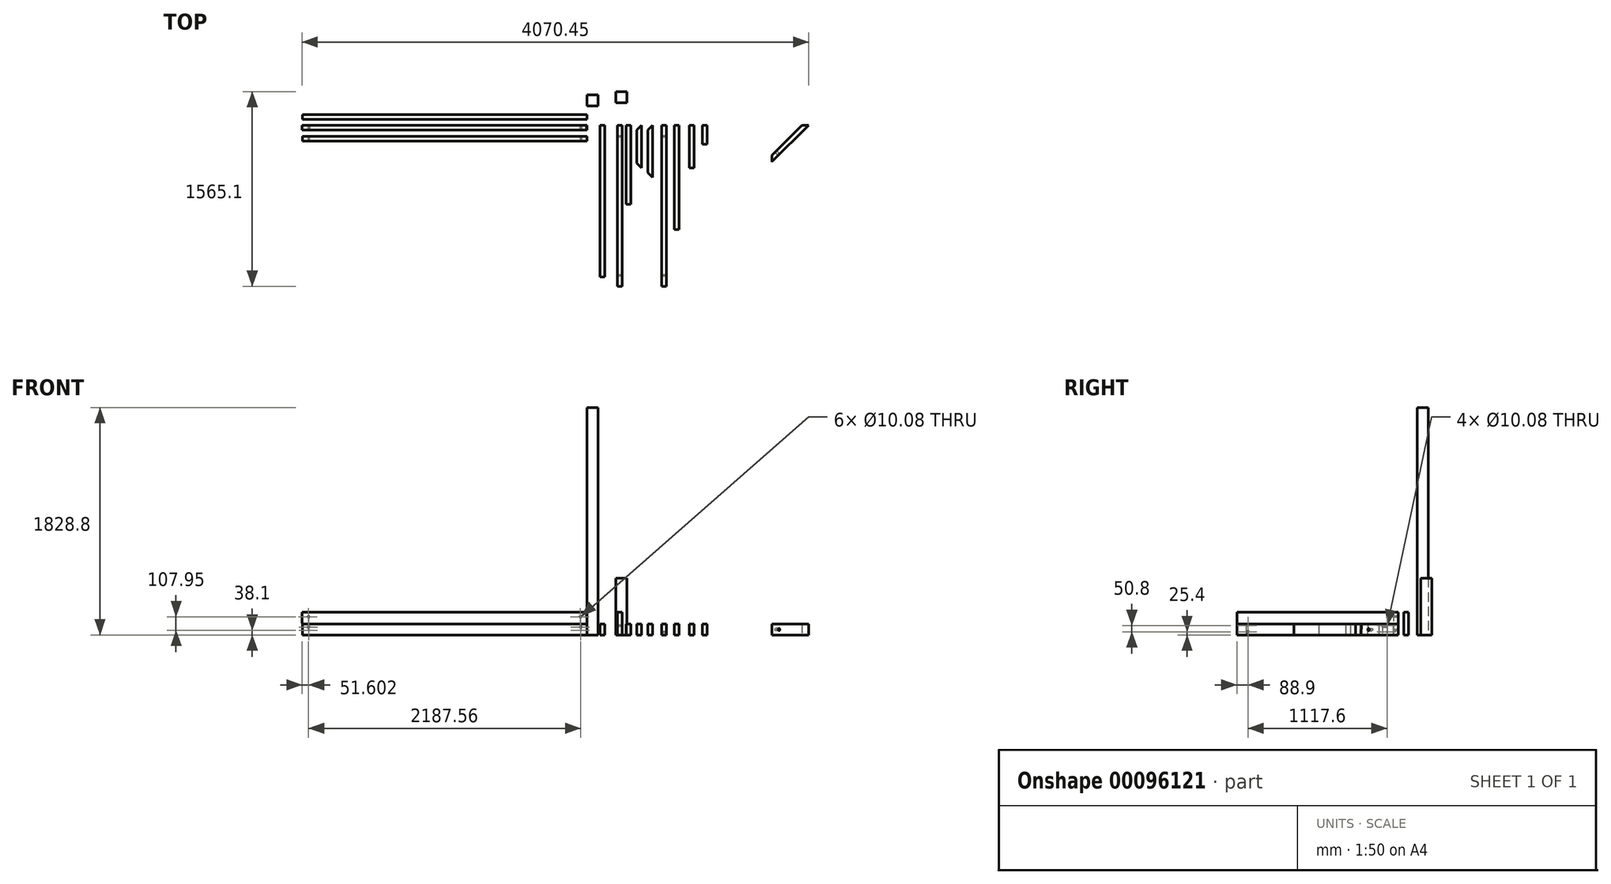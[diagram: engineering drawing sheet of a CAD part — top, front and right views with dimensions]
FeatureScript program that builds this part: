
annotation { "Feature Type Name" : "Feature", "Feature Type Description" : "" }
export const myFeature = defineFeature(function(context is Context, id is Id, definition is map)
    precondition{}
    {
        {
            var Q0;
            Q0=qCreatedBy(makeId("Right.planeOp"),FACE);
            var sketch = newSketch(context, id + "F0", { "sketchPlane" : qUnion([Q0])});
            skLineSegment(sketch, "E0.bottom", {"start": v(0, 0) * mm, "end": v(-38.1, 0) * mm});
            skLineSegment(sketch, "E0.top", {"start": v(0, 184.15) * mm, "end": v(-38.1, 184.15) * mm});
            skLineSegment(sketch, "E0.left", {"start": v(0, 0) * mm, "end": v(0, 184.15) * mm});
            skLineSegment(sketch, "E0.right", {"start": v(-38.1, 0) * mm, "end": v(-38.1, 184.15) * mm});
            skSolve(sketch);
        }
        {
            var Q0;
            Q0=makeQuery(id+"F0.imprint","IMPRINT",FACE,{"disambiguationData":[TD([[makeQuery(id+"F0.imprint","IMPRINT",EDGE,{"derivedFrom":sQuery(id+"F0.wireOp",EDGE,"E0.bottom")}),-1.0]])]});
            extrude(context, id + "F1", {"entities" : qUnion([Q0]), "oppositeDirection" : true, "depth" : 2289.96 * mm});
        }
        {
            var Q0;
            Q0=makeQuery(id+"F1.opExtrude","SWEPT_FACE",FACE,{"disambiguationData":[OSD([sQuery(id+"F0.wireOp",EDGE,"E0.right")])]});
            var sketch = newSketch(context, id + "F2", { "sketchPlane" : qUnion([Q0])});
            skLineSegment(sketch, "E1", {"start": v(0, 0) * mm, "end": v(0, 184.15) * mm});
            skLineSegment(sketch, "E2", {"start": v(0, 184.15) * mm, "end": v(-3.84, 184.15) * mm});
            skLineSegment(sketch, "E3", {"start": v(-3.84, 184.15) * mm, "end": v(0, 0) * mm});
            skLineSegment(sketch, "E4", {"start": v(-2289.96, 184.15) * mm, "end": v(-2286.13, 0) * mm});
            skLineSegment(sketch, "E5", {"start": v(-2286.13, 0) * mm, "end": v(-2289.96, 0) * mm});
            skLineSegment(sketch, "E6", {"start": v(-2289.96, 0) * mm, "end": v(-2289.96, 184.15) * mm});
            skSolve(sketch);
        }
        {
            var Q0;
            Q0=qSketchRegion(id+"F2",true);
            extrude(context, id + "F3", {"entities" : qUnion([Q0]), "operationType" : NewBodyOperationType.REMOVE, "oppositeDirection" : true, "depth" : 38.1 * mm});
        }
        {
            var Q0;
            Q0=qCreatedBy(makeId("Front.planeOp"),FACE);
            var sketch = newSketch(context, id + "F4", { "sketchPlane" : qUnion([Q0])});
            skLineSegment(sketch, "E7.bottom", {"start": v(103.6, 0) * mm, "end": v(141.7, 0) * mm});
            skLineSegment(sketch, "E7.top", {"start": v(103.6, 88.9) * mm, "end": v(141.7, 88.9) * mm});
            skLineSegment(sketch, "E7.left", {"start": v(103.6, 0) * mm, "end": v(103.6, 88.9) * mm});
            skLineSegment(sketch, "E7.right", {"start": v(141.7, 0) * mm, "end": v(141.7, 88.9) * mm});
            skSolve(sketch);
        }
        {
            var Q0;
            Q0=makeQuery(id+"F4.imprint","IMPRINT",FACE,{"disambiguationData":[TD([[makeQuery(id+"F4.imprint","IMPRINT",EDGE,{"derivedFrom":sQuery(id+"F4.wireOp",EDGE,"E7.bottom")}),1.0]])]});
            extrude(context, id + "F5", {"entities" : qUnion([Q0]), "depth" : 1219.2 * mm});
        }
        {
            var Q0;
            Q0=qCreatedBy(makeId("Top.planeOp"),FACE);
            var sketch = newSketch(context, id + "F6", { "sketchPlane" : qUnion([Q0])});
            skLineSegment(sketch, "E8.bottom", {"start": v(0, 155.1) * mm, "end": v(88.9, 155.1) * mm});
            skLineSegment(sketch, "E8.top", {"start": v(0, 244) * mm, "end": v(88.9, 244) * mm});
            skLineSegment(sketch, "E8.left", {"start": v(0, 155.1) * mm, "end": v(0, 244) * mm});
            skLineSegment(sketch, "E8.right", {"start": v(88.9, 155.1) * mm, "end": v(88.9, 244) * mm});
            skSolve(sketch);
        }
        {
            var Q0;
            Q0=qSketchRegion(id+"F6",true);
            extrude(context, id + "F7", {"entities" : qUnion([Q0]), "depth" : 1828.8 * mm});
        }
        {
            var Q0;
            Q0=qCreatedBy(makeId("Front.planeOp"),FACE);
            var sketch = newSketch(context, id + "F8", { "sketchPlane" : qUnion([Q0])});
            skLineSegment(sketch, "E9.bottom", {"start": v(244.55, 0) * mm, "end": v(282.65, 0) * mm});
            skLineSegment(sketch, "E9.top", {"start": v(244.55, 184.15) * mm, "end": v(282.65, 184.15) * mm});
            skLineSegment(sketch, "E9.left", {"start": v(244.55, 0) * mm, "end": v(244.55, 184.15) * mm});
            skLineSegment(sketch, "E9.right", {"start": v(282.65, 0) * mm, "end": v(282.65, 184.15) * mm});
            skSolve(sketch);
        }
        {
            var Q0;
            Q0=makeQuery(id+"F8.imprint","IMPRINT",FACE,{"disambiguationData":[TD([[makeQuery(id+"F8.imprint","IMPRINT",EDGE,{"derivedFrom":sQuery(id+"F8.wireOp",EDGE,"E9.bottom")}),1.0]])]});
            extrude(context, id + "F9", {"entities" : qUnion([Q0]), "depth" : 1295.4 * mm});
        }
        {
            var Q0;
            Q0=qCreatedBy(makeId("Front.planeOp"),FACE);
            var sketch = newSketch(context, id + "F10", { "sketchPlane" : qUnion([Q0])});
            skLineSegment(sketch, "E10.bottom", {"start": v(312.63, 0) * mm, "end": v(350.73, 0) * mm});
            skLineSegment(sketch, "E10.top", {"start": v(312.63, 88.9) * mm, "end": v(350.73, 88.9) * mm});
            skLineSegment(sketch, "E10.left", {"start": v(312.63, 0) * mm, "end": v(312.63, 88.9) * mm});
            skLineSegment(sketch, "E10.right", {"start": v(350.73, 0) * mm, "end": v(350.73, 88.9) * mm});
            skSolve(sketch);
        }
        {
            var Q0;
            Q0=makeQuery(id+"F10.imprint","IMPRINT",FACE,{"disambiguationData":[TD([[makeQuery(id+"F10.imprint","IMPRINT",EDGE,{"derivedFrom":sQuery(id+"F10.wireOp",EDGE,"E10.bottom")}),1.0]])]});
            extrude(context, id + "F11", {"entities" : qUnion([Q0]), "depth" : 635 * mm});
        }
        {
            var Q0;
            Q0=makeQuery(id+"F1.opExtrude","SWEPT_FACE",FACE,{"disambiguationData":[OSD([sQuery(id+"F0.wireOp",EDGE,"E0.right")])]});
            var sketch = newSketch(context, id + "F12", { "sketchPlane" : qUnion([Q0])});
            skPoint(sketch, "E11", {"position": v(-2238.36, 146.05) * mm});
            skPoint(sketch, "E12", {"position": v(-2236.1, 38.1) * mm});
            skPoint(sketch, "E13", {"position": v(-53.85, 146.05) * mm});
            skPoint(sketch, "E14", {"position": v(-51.6, 38.1) * mm});
            skSolve(sketch);
        }
        {
            var Q0;
            Q0=sQuery(id+"F12.wireOp",VERTEX,"E14");
            var Q1;
            Q1=sQuery(id+"F12.wireOp",VERTEX,"E13");
            var Q2;
            Q2=sQuery(id+"F12.wireOp",VERTEX,"E12");
            var Q3;
            Q3=sQuery(id+"F12.wireOp",VERTEX,"E11");
            var Q4;
            Q4=makeQuery(id+"F1.opExtrude","SWEPT_BODY",BODY,{"disambiguationData":[OSD([sQuery(id+"F0.wireOp",EDGE,"E0.bottom"),sQuery(id+"F0.wireOp",EDGE,"E0.top"),sQuery(id+"F0.wireOp",EDGE,"E0.left"),sQuery(id+"F0.wireOp",EDGE,"E0.right")])]});
            hole(context, id + "F13", {"style" : HoleStyle.SIMPLE, "endStyle" : HoleEndStyle.THROUGH, "standardTappedOrClearance" : lookupTablePath({ "standard" : "ANSI", "fit" : "Normal (ASME)", "size" : "3/8", "type" : "Clearance" }), "standardBlindInLast" : lookupTablePath({ "fit" : "Free", "standard" : "ANSI", "size" : "3/8", "type" : "Clearance" }), "holeDiameter" : 10.08 * mm, "locations" : qUnion([Q0, Q1, Q2, Q3]), "scope" : qUnion([Q4]), "isTappedThrough" : true});
        }
        {
            var Q0;
            Q0=makeQuery(id+"F9.opExtrude","SWEPT_FACE",FACE,{"disambiguationData":[OSD([sQuery(id+"F8.wireOp",EDGE,"E9.right")])]});
            var sketch = newSketch(context, id + "F14", { "sketchPlane" : qUnion([Q0])});
            skPoint(sketch, "E15", {"position": v(-1206.5, 76.2) * mm});
            skPoint(sketch, "E16", {"position": v(-88.9, 76.2) * mm});
            skSolve(sketch);
        }
        {
            var Q0;
            Q0=sQuery(id+"F14.wireOp",VERTEX,"4c446d8b-93f8-499f-88b7-25f558c8394a");
            var Q1;
            Q1=sQuery(id+"F14.wireOp",VERTEX,"E15");
            var Q2;
            Q2=sQuery(id+"F14.wireOp",VERTEX,"E16");
            var Q3;
            Q3=sQuery(id+"F14.wireOp",VERTEX,"ef1d34a0-cfd4-4a64-a352-8786edb42035");
            var Q4;
            Q4=makeQuery(id+"F9.opExtrude","SWEPT_BODY",BODY,{"disambiguationData":[OSD([sQuery(id+"F8.wireOp",EDGE,"E9.bottom"),sQuery(id+"F8.wireOp",EDGE,"E9.top"),sQuery(id+"F8.wireOp",EDGE,"E9.left"),sQuery(id+"F8.wireOp",EDGE,"E9.right")])]});
            hole(context, id + "F15", {"style" : HoleStyle.SIMPLE, "endStyle" : HoleEndStyle.THROUGH, "standardTappedOrClearance" : lookupTablePath({ "standard" : "ANSI", "fit" : "Normal (ASME)", "size" : "3/8", "type" : "Clearance" }), "standardBlindInLast" : lookupTablePath({ "fit" : "Free", "standard" : "ANSI", "size" : "3/8", "type" : "Clearance" }), "holeDiameter" : 10.08 * mm, "locations" : qUnion([Q0, Q1, Q2, Q3]), "scope" : qUnion([Q4]), "isTappedThrough" : true});
        }
        {
            var Q0;
            Q0=qCreatedBy(makeId("Front.planeOp"),FACE);
            var sketch = newSketch(context, id + "F16", { "sketchPlane" : qUnion([Q0])});
            skLineSegment(sketch, "E17.bottom", {"start": v(399.52, 0) * mm, "end": v(437.62, 0) * mm});
            skLineSegment(sketch, "E17.top", {"start": v(399.52, 88.9) * mm, "end": v(437.62, 88.9) * mm});
            skLineSegment(sketch, "E17.left", {"start": v(399.52, 0) * mm, "end": v(399.52, 88.9) * mm});
            skLineSegment(sketch, "E17.right", {"start": v(437.62, 0) * mm, "end": v(437.62, 88.9) * mm});
            skSolve(sketch);
        }
        {
            var Q0;
            Q0=makeQuery(id+"F16.imprint","IMPRINT",FACE,{"disambiguationData":[TD([[makeQuery(id+"F16.imprint","IMPRINT",EDGE,{"derivedFrom":sQuery(id+"F16.wireOp",EDGE,"E17.bottom")}),1.0]])]});
            extrude(context, id + "F17", {"entities" : qUnion([Q0]), "depth" : 342.9 * mm});
        }
        {
            var Q0;
            Q0=makeQuery(id+"F17.opExtrude","SWEPT_FACE",FACE,{"disambiguationData":[OSD([sQuery(id+"F16.wireOp",EDGE,"E17.top")])]});
            var sketch = newSketch(context, id + "F18", { "sketchPlane" : qUnion([Q0])});
            skLineSegment(sketch, "E18", {"start": v(437.62, 0) * mm, "end": v(399.52, -38.1) * mm});
            skLineSegment(sketch, "E19", {"start": v(399.52, -38.1) * mm, "end": v(399.52, 0) * mm});
            skLineSegment(sketch, "E20", {"start": v(399.52, 0) * mm, "end": v(437.62, 0) * mm});
            skLineSegment(sketch, "E21", {"start": v(437.62, -342.9) * mm, "end": v(399.52, -304.8) * mm});
            skLineSegment(sketch, "E22", {"start": v(399.52, -304.8) * mm, "end": v(399.52, -342.9) * mm});
            skLineSegment(sketch, "E23", {"start": v(399.52, -342.9) * mm, "end": v(437.62, -342.9) * mm});
            skSolve(sketch);
        }
        {
            var Q0;
            Q0=makeQuery(id+"F18.imprint","IMPRINT",FACE,{"disambiguationData":[TD([[makeQuery(id+"F18.imprint","IMPRINT",EDGE,{"derivedFrom":sQuery(id+"F18.wireOp",EDGE,"E18")}),-1.0]])]});
            var Q1;
            Q1=makeQuery(id+"F18.imprint","IMPRINT",FACE,{"disambiguationData":[TD([[makeQuery(id+"F18.imprint","IMPRINT",EDGE,{"derivedFrom":sQuery(id+"F18.wireOp",EDGE,"E21")}),1.0]])]});
            extrude(context, id + "F19", {"entities" : qUnion([Q0, Q1]), "operationType" : NewBodyOperationType.REMOVE, "oppositeDirection" : true, "depth" : 88.9 * mm});
        }
        {
            var Q0;
            Q0=qCreatedBy(makeId("Top.planeOp"),FACE);
            var sketch = newSketch(context, id + "F20", { "sketchPlane" : qUnion([Q0])});
            skLineSegment(sketch, "E24.bottom", {"start": v(230.08, 180.8) * mm, "end": v(318.98, 180.8) * mm});
            skLineSegment(sketch, "E24.top", {"start": v(230.08, 269.7) * mm, "end": v(318.98, 269.7) * mm});
            skLineSegment(sketch, "E24.left", {"start": v(230.08, 180.8) * mm, "end": v(230.08, 269.7) * mm});
            skLineSegment(sketch, "E24.right", {"start": v(318.98, 180.8) * mm, "end": v(318.98, 269.7) * mm});
            skSolve(sketch);
        }
        {
            var Q0;
            Q0=makeQuery(id+"F20.imprint","IMPRINT",FACE,{"disambiguationData":[TD([[makeQuery(id+"F20.imprint","IMPRINT",EDGE,{"derivedFrom":sQuery(id+"F20.wireOp",EDGE,"E24.bottom")}),1.0]])]});
            extrude(context, id + "F21", {"entities" : qUnion([Q0]), "depth" : 457.2 * mm});
        }
        {
            var Q0;
            Q0=qCreatedBy(makeId("Front.planeOp"),FACE);
            var sketch = newSketch(context, id + "F22", { "sketchPlane" : qUnion([Q0])});
            skLineSegment(sketch, "E25.bottom", {"start": v(487.43, 0) * mm, "end": v(525.53, 0) * mm});
            skLineSegment(sketch, "E25.top", {"start": v(487.43, 88.9) * mm, "end": v(525.53, 88.9) * mm});
            skLineSegment(sketch, "E25.left", {"start": v(487.43, 0) * mm, "end": v(487.43, 88.9) * mm});
            skLineSegment(sketch, "E25.right", {"start": v(525.53, 0) * mm, "end": v(525.53, 88.9) * mm});
            skSolve(sketch);
        }
        {
            var Q0;
            Q0=makeQuery(id+"F22.imprint","IMPRINT",FACE,{"disambiguationData":[TD([[makeQuery(id+"F22.imprint","IMPRINT",EDGE,{"derivedFrom":sQuery(id+"F22.wireOp",EDGE,"E25.bottom")}),1.0]])]});
            extrude(context, id + "F23", {"entities" : qUnion([Q0]), "depth" : 419.1 * mm});
        }
        {
            var Q0;
            Q0=makeQuery(id+"F23.opExtrude","SWEPT_FACE",FACE,{"disambiguationData":[OSD([sQuery(id+"F22.wireOp",EDGE,"E25.top")])]});
            var sketch = newSketch(context, id + "F24", { "sketchPlane" : qUnion([Q0])});
            skLineSegment(sketch, "E26", {"start": v(525.53, 0) * mm, "end": v(525.53, 38.1) * mm});
            skLineSegment(sketch, "E27", {"start": v(525.53, 38.1) * mm, "end": v(487.43, 0) * mm});
            skLineSegment(sketch, "E28", {"start": v(487.43, 0) * mm, "end": v(525.53, 0) * mm});
            skLineSegment(sketch, "E29", {"start": v(525.53, -419.1) * mm, "end": v(525.53, -457.2) * mm});
            skLineSegment(sketch, "E30", {"start": v(525.53, -457.2) * mm, "end": v(487.43, -419.1) * mm});
            skLineSegment(sketch, "E31", {"start": v(487.43, -419.1) * mm, "end": v(525.53, -419.1) * mm});
            skSolve(sketch);
        }
        {
            var Q0;
            Q0=makeQuery(id+"F24.imprint","IMPRINT",FACE,{"disambiguationData":[TD([[makeQuery(id+"F24.imprint","IMPRINT",EDGE,{"derivedFrom":sQuery(id+"F24.wireOp",EDGE,"E26")}),1.0]])]});
            var Q1;
            Q1=makeQuery(id+"F24.imprint","IMPRINT",FACE,{"disambiguationData":[TD([[makeQuery(id+"F24.imprint","IMPRINT",EDGE,{"derivedFrom":sQuery(id+"F24.wireOp",EDGE,"E29")}),-1.0]])]});
            extrude(context, id + "F25", {"entities" : qUnion([Q0, Q1]), "oppositeDirection" : true, "depth" : 88.9 * mm});
        }
        {
            var Q0;
            Q0=makeQuery(id+"F25.opExtrude","SWEPT_BODY",BODY,{"disambiguationData":[OSD([sQuery(id+"F24.wireOp",EDGE,"E29"),sQuery(id+"F24.wireOp",EDGE,"E30"),sQuery(id+"F24.wireOp",EDGE,"E31")])]});
            deleteBodies(context, id + "F26", {"entities" : qUnion([Q0])});
        }
        {
            var Q0;
            Q0=makeQuery(id+"F25.opExtrude","SWEPT_BODY",BODY,{"disambiguationData":[OSD([sQuery(id+"F24.wireOp",EDGE,"E26"),sQuery(id+"F24.wireOp",EDGE,"E27"),sQuery(id+"F24.wireOp",EDGE,"E28")])]});
            deleteBodies(context, id + "F27", {"entities" : qUnion([Q0])});
        }
        {
            var Q0;
            Q0=makeQuery(id+"F23.opExtrude","SWEPT_FACE",FACE,{"disambiguationData":[OSD([sQuery(id+"F22.wireOp",EDGE,"E25.top")])]});
            var sketch = newSketch(context, id + "F28", { "sketchPlane" : qUnion([Q0])});
            skLineSegment(sketch, "E32", {"start": v(525.53, 0) * mm, "end": v(487.43, -38.1) * mm});
            skLineSegment(sketch, "E33", {"start": v(487.43, -38.1) * mm, "end": v(487.43, 0) * mm});
            skLineSegment(sketch, "E34", {"start": v(487.43, 0) * mm, "end": v(525.53, 0) * mm});
            skLineSegment(sketch, "E35", {"start": v(525.53, -419.1) * mm, "end": v(487.43, -381) * mm});
            skLineSegment(sketch, "E36", {"start": v(487.43, -381) * mm, "end": v(487.43, -419.1) * mm});
            skLineSegment(sketch, "E37", {"start": v(487.43, -419.1) * mm, "end": v(525.53, -419.1) * mm});
            skSolve(sketch);
        }
        {
            var Q0;
            Q0=makeQuery(id+"F28.imprint","IMPRINT",FACE,{"disambiguationData":[TD([[makeQuery(id+"F28.imprint","IMPRINT",EDGE,{"derivedFrom":sQuery(id+"F28.wireOp",EDGE,"E32")}),-1.0]])]});
            var Q1;
            Q1=makeQuery(id+"F28.imprint","IMPRINT",FACE,{"disambiguationData":[TD([[makeQuery(id+"F28.imprint","IMPRINT",EDGE,{"derivedFrom":sQuery(id+"F28.wireOp",EDGE,"E35")}),1.0]])]});
            extrude(context, id + "F29", {"entities" : qUnion([Q0, Q1]), "operationType" : NewBodyOperationType.REMOVE, "oppositeDirection" : true, "depth" : 88.9 * mm});
        }
        {
            var Q0;
            Q0=qCreatedBy(makeId("Right.planeOp"),FACE);
            var sketch = newSketch(context, id + "F30", { "sketchPlane" : qUnion([Q0])});
            skLineSegment(sketch, "E38.bottom", {"start": v(-88.17, 0) * mm, "end": v(-126.27, 0) * mm});
            skLineSegment(sketch, "E38.top", {"start": v(-88.17, 88.9) * mm, "end": v(-126.27, 88.9) * mm});
            skLineSegment(sketch, "E38.left", {"start": v(-88.17, 0) * mm, "end": v(-88.17, 88.9) * mm});
            skLineSegment(sketch, "E38.right", {"start": v(-126.27, 0) * mm, "end": v(-126.27, 88.9) * mm});
            skSolve(sketch);
        }
        {
            var Q0;
            Q0=makeQuery(id+"F30.imprint","IMPRINT",FACE,{"disambiguationData":[TD([[makeQuery(id+"F30.imprint","IMPRINT",EDGE,{"derivedFrom":sQuery(id+"F30.wireOp",EDGE,"E38.bottom")}),-1.0]])]});
            extrude(context, id + "F31", {"entities" : qUnion([Q0]), "oppositeDirection" : true, "depth" : 2287.9 * mm});
        }
        {
            var Q0;
            Q0=makeQuery(id+"F31.opExtrude","SWEPT_FACE",FACE,{"disambiguationData":[OSD([sQuery(id+"F30.wireOp",EDGE,"E38.right")])]});
            var sketch = newSketch(context, id + "F32", { "sketchPlane" : qUnion([Q0])});
            skLineSegment(sketch, "E39", {"start": v(0, 0) * mm, "end": v(-1.85, 88.9) * mm});
            skLineSegment(sketch, "E40", {"start": v(-1.85, 88.9) * mm, "end": v(0, 88.9) * mm});
            skLineSegment(sketch, "E41", {"start": v(0, 88.9) * mm, "end": v(0, 0) * mm});
            skLineSegment(sketch, "E42", {"start": v(-2287.91, 88.9) * mm, "end": v(-2286.06, 0) * mm});
            skLineSegment(sketch, "E43", {"start": v(-2286.06, 0) * mm, "end": v(-2287.91, 0) * mm});
            skLineSegment(sketch, "E44", {"start": v(-2287.91, 0) * mm, "end": v(-2287.91, 88.9) * mm});
            skSolve(sketch);
        }
        {
            var Q0;
            Q0=makeQuery(id+"F32.imprint","IMPRINT",FACE,{"disambiguationData":[TD([[makeQuery(id+"F32.imprint","IMPRINT",EDGE,{"derivedFrom":sQuery(id+"F32.wireOp",EDGE,"E42")}),-1.0]])]});
            var Q1;
            Q1=makeQuery(id+"F32.imprint","IMPRINT",FACE,{"disambiguationData":[TD([[makeQuery(id+"F32.imprint","IMPRINT",EDGE,{"derivedFrom":sQuery(id+"F32.wireOp",EDGE,"E39")}),-1.0]])]});
            extrude(context, id + "F33", {"entities" : qUnion([Q0, Q1]), "operationType" : NewBodyOperationType.REMOVE, "oppositeDirection" : true, "depth" : 38.1 * mm});
        }
        {
            var Q0;
            Q0=qCreatedBy(makeId("Front.planeOp"),FACE);
            var sketch = newSketch(context, id + "F34", { "sketchPlane" : qUnion([Q0])});
            skLineSegment(sketch, "E45.bottom", {"start": v(600.5, 0) * mm, "end": v(638.6, 0) * mm});
            skLineSegment(sketch, "E45.top", {"start": v(600.5, 88.9) * mm, "end": v(638.6, 88.9) * mm});
            skLineSegment(sketch, "E45.left", {"start": v(600.5, 0) * mm, "end": v(600.5, 88.9) * mm});
            skLineSegment(sketch, "E45.right", {"start": v(638.6, 0) * mm, "end": v(638.6, 88.9) * mm});
            skSolve(sketch);
        }
        {
            var Q0;
            Q0=makeQuery(id+"F34.imprint","IMPRINT",FACE,{"disambiguationData":[TD([[makeQuery(id+"F34.imprint","IMPRINT",EDGE,{"derivedFrom":sQuery(id+"F34.wireOp",EDGE,"E45.bottom")}),1.0]])]});
            extrude(context, id + "F35", {"entities" : qUnion([Q0]), "depth" : 1295.4 * mm});
        }
        {
            var Q0;
            Q0=makeQuery(id+"F31.opExtrude","SWEPT_FACE",FACE,{"disambiguationData":[OSD([sQuery(id+"F30.wireOp",EDGE,"E38.right")])]});
            var sketch = newSketch(context, id + "F36", { "sketchPlane" : qUnion([Q0])});
            skPoint(sketch, "E46", {"position": v(-2237.11, 63.5) * mm});
            skPoint(sketch, "E47", {"position": v(-50.8, 63.5) * mm});
            skSolve(sketch);
        }
        {
            var Q0;
            Q0=sQuery(id+"F36.wireOp",VERTEX,"E46");
            var Q1;
            Q1=sQuery(id+"F36.wireOp",VERTEX,"E47");
            var Q2;
            Q2=makeQuery(id+"F31.opExtrude","SWEPT_BODY",BODY,{"disambiguationData":[OSD([sQuery(id+"F30.wireOp",EDGE,"E38.bottom"),sQuery(id+"F30.wireOp",EDGE,"E38.top"),sQuery(id+"F30.wireOp",EDGE,"E38.left"),sQuery(id+"F30.wireOp",EDGE,"E38.right")])]});
            hole(context, id + "F37", {"style" : HoleStyle.SIMPLE, "endStyle" : HoleEndStyle.THROUGH, "standardTappedOrClearance" : lookupTablePath({ "standard" : "ANSI", "fit" : "Normal (ASME)", "size" : "3/8", "type" : "Clearance" }), "standardBlindInLast" : lookupTablePath({ "fit" : "Free", "standard" : "ANSI", "size" : "3/8", "type" : "Clearance" }), "holeDiameter" : 10.08 * mm, "locations" : qUnion([Q0, Q1]), "scope" : qUnion([Q2]), "isTappedThrough" : true});
        }
        {
            var Q0;
            Q0=makeQuery(id+"F35.opExtrude","SWEPT_FACE",FACE,{"disambiguationData":[OSD([sQuery(id+"F34.wireOp",EDGE,"E45.right")])]});
            var sketch = newSketch(context, id + "F38", { "sketchPlane" : qUnion([Q0])});
            skPoint(sketch, "E48", {"position": v(-1206.5, 25.4) * mm});
            skPoint(sketch, "E49", {"position": v(-88.9, 25.4) * mm});
            skSolve(sketch);
        }
        {
            var Q0;
            Q0=sQuery(id+"F38.wireOp",VERTEX,"E49");
            var Q1;
            Q1=sQuery(id+"F38.wireOp",VERTEX,"E48");
            var Q2;
            Q2=makeQuery(id+"F35.opExtrude","SWEPT_BODY",BODY,{"disambiguationData":[OSD([sQuery(id+"F34.wireOp",EDGE,"E45.bottom"),sQuery(id+"F34.wireOp",EDGE,"E45.top"),sQuery(id+"F34.wireOp",EDGE,"E45.left"),sQuery(id+"F34.wireOp",EDGE,"E45.right")])]});
            hole(context, id + "F39", {"style" : HoleStyle.SIMPLE, "endStyle" : HoleEndStyle.THROUGH, "standardTappedOrClearance" : lookupTablePath({ "standard" : "ANSI", "fit" : "Normal (ASME)", "size" : "3/8", "type" : "Clearance" }), "standardBlindInLast" : lookupTablePath({ "fit" : "Free", "standard" : "ANSI", "size" : "3/8", "type" : "Clearance" }), "holeDiameter" : 10.08 * mm, "locations" : qUnion([Q0, Q1]), "scope" : qUnion([Q2]), "isTappedThrough" : true});
        }
        {
            var Q0;
            Q0=qCreatedBy(makeId("Front.planeOp"),FACE);
            var sketch = newSketch(context, id + "F40", { "sketchPlane" : qUnion([Q0])});
            skLineSegment(sketch, "E50.bottom", {"start": v(700.78, 0) * mm, "end": v(738.88, 0) * mm});
            skLineSegment(sketch, "E50.top", {"start": v(700.78, 88.9) * mm, "end": v(738.88, 88.9) * mm});
            skLineSegment(sketch, "E50.left", {"start": v(700.78, 0) * mm, "end": v(700.78, 88.9) * mm});
            skLineSegment(sketch, "E50.right", {"start": v(738.88, 0) * mm, "end": v(738.88, 88.9) * mm});
            skSolve(sketch);
        }
        {
            var Q0;
            Q0=makeQuery(id+"F40.imprint","IMPRINT",FACE,{"disambiguationData":[TD([[makeQuery(id+"F40.imprint","IMPRINT",EDGE,{"derivedFrom":sQuery(id+"F40.wireOp",EDGE,"E50.bottom")}),1.0]])]});
            extrude(context, id + "F41", {"entities" : qUnion([Q0]), "depth" : 838.2 * mm});
        }
        {
            var Q0;
            Q0=qCreatedBy(makeId("Front.planeOp"),FACE);
            var sketch = newSketch(context, id + "F42", { "sketchPlane" : qUnion([Q0])});
            skLineSegment(sketch, "E51.bottom", {"start": v(821.33, 88.9) * mm, "end": v(859.43, 88.9) * mm});
            skLineSegment(sketch, "E51.top", {"start": v(821.33, 0) * mm, "end": v(859.43, 0) * mm});
            skLineSegment(sketch, "E51.left", {"start": v(821.33, 88.9) * mm, "end": v(821.33, 0) * mm});
            skLineSegment(sketch, "E51.right", {"start": v(859.43, 88.9) * mm, "end": v(859.43, 0) * mm});
            skSolve(sketch);
        }
        {
            var Q0;
            Q0=makeQuery(id+"F42.imprint","IMPRINT",FACE,{"disambiguationData":[TD([[makeQuery(id+"F42.imprint","IMPRINT",EDGE,{"derivedFrom":sQuery(id+"F42.wireOp",EDGE,"E51.bottom")}),-1.0]])]});
            extrude(context, id + "F43", {"entities" : qUnion([Q0]), "depth" : 342.9 * mm});
        }
        {
            var Q0;
            Q0=makeQuery(id+"F43.opExtrude","SWEPT_FACE",FACE,{"disambiguationData":[OSD([sQuery(id+"F42.wireOp",EDGE,"E51.right")])]});
            var sketch = newSketch(context, id + "F44", { "sketchPlane" : qUnion([Q0])});
            skLineSegment(sketch, "E52", {"start": v(-342.9, 88.9) * mm, "end": v(-341.04, 0) * mm});
            skLineSegment(sketch, "E53", {"start": v(-341.04, 0) * mm, "end": v(-342.9, 0) * mm});
            skLineSegment(sketch, "E54", {"start": v(-342.9, 0) * mm, "end": v(-342.9, 88.9) * mm});
            skSolve(sketch);
        }
        {
            var Q0;
            Q0=makeQuery(id+"F44.imprint","IMPRINT",FACE,{"disambiguationData":[TD([[makeQuery(id+"F44.imprint","IMPRINT",EDGE,{"derivedFrom":sQuery(id+"F44.wireOp",EDGE,"E52")}),-1.0]])]});
            extrude(context, id + "F45", {"entities" : qUnion([Q0]), "operationType" : NewBodyOperationType.REMOVE, "oppositeDirection" : true, "depth" : 38.1 * mm});
        }
        {
            var Q0;
            Q0=qCreatedBy(makeId("Front.planeOp"),FACE);
            var sketch = newSketch(context, id + "F46", { "sketchPlane" : qUnion([Q0])});
            skLineSegment(sketch, "E55.bottom", {"start": v(926.3, 0) * mm, "end": v(964.4, 0) * mm});
            skLineSegment(sketch, "E55.top", {"start": v(926.3, 88.9) * mm, "end": v(964.4, 88.9) * mm});
            skLineSegment(sketch, "E55.left", {"start": v(926.3, 0) * mm, "end": v(926.3, 88.9) * mm});
            skLineSegment(sketch, "E55.right", {"start": v(964.4, 0) * mm, "end": v(964.4, 88.9) * mm});
            skSolve(sketch);
        }
        {
            var Q0;
            Q0=makeQuery(id+"F46.imprint","IMPRINT",FACE,{"disambiguationData":[TD([[makeQuery(id+"F46.imprint","IMPRINT",EDGE,{"derivedFrom":sQuery(id+"F46.wireOp",EDGE,"E55.bottom")}),1.0]])]});
            extrude(context, id + "F47", {"entities" : qUnion([Q0]), "depth" : 152.4 * mm});
        }
        {
            var Q0;
            Q0=qCreatedBy(makeId("Top.planeOp"),FACE);
            var sketch = newSketch(context, id + "F48", { "sketchPlane" : qUnion([Q0])});
            skLineSegment(sketch, "E56", {"start": v(1780.5, 0) * mm, "end": v(1726.6, 0) * mm});
            skLineSegment(sketch, "E57", {"start": v(1726.6, 0) * mm, "end": v(1484.14, -242.47) * mm});
            skLineSegment(sketch, "E58", {"start": v(1484.14, -242.47) * mm, "end": v(1484.14, -296.35) * mm});
            skLineSegment(sketch, "E59", {"start": v(1484.14, -296.35) * mm, "end": v(1780.5, 0) * mm});
            skSolve(sketch);
        }
        {
            var Q0;
            Q0=makeQuery(id+"F48.imprint","IMPRINT",FACE,{"disambiguationData":[TD([[makeQuery(id+"F48.imprint","IMPRINT",EDGE,{"derivedFrom":sQuery(id+"F48.wireOp",EDGE,"E56")}),1.0]])]});
            extrude(context, id + "F49", {"entities" : qUnion([Q0]), "depth" : 88.9 * mm});
        }
        {
            var Q0;
            Q0=qCreatedBy(makeId("Front.planeOp"),FACE);
            var sketch = newSketch(context, id + "F50", { "sketchPlane" : qUnion([Q0])});
            skLineSegment(sketch, "E60", {"start": v(1484.14, 0) * mm, "end": v(1484.14, 89.06) * mm});
            skLineSegment(sketch, "E61", {"start": v(1484.14, 89.06) * mm, "end": v(1486, 89.06) * mm});
            skLineSegment(sketch, "E62", {"start": v(1486, 89.06) * mm, "end": v(1484.14, 0) * mm});
            skSolve(sketch);
        }
        {
            var Q0;
            Q0=makeQuery(id+"F50.imprint","IMPRINT",FACE,{"disambiguationData":[TD([[makeQuery(id+"F50.imprint","IMPRINT",EDGE,{"derivedFrom":sQuery(id+"F50.wireOp",EDGE,"E60")}),-1.0]])]});
            extrude(context, id + "F51", {"entities" : qUnion([Q0]), "operationType" : NewBodyOperationType.REMOVE, "depth" : 508 * mm});
        }
        {
            var Q0;
            Q0=makeQuery(id+"F49.opExtrude","SWEPT_FACE",FACE,{"disambiguationData":[OSD([sQuery(id+"F48.wireOp",EDGE,"E57")])]});
            var sketch = newSketch(context, id + "F52", { "sketchPlane" : qUnion([Q0])});
            skCircle(sketch, "E63", {"center": v(-922.82, 43.84) * mm, "radius": 9.14 * mm});
            skSolve(sketch);
        }
        {
            var Q0;
            Q0=makeQuery(id+"F52.imprint","IMPRINT",FACE,{"disambiguationData":[TD([[makeQuery(id+"F52.imprint","IMPRINT",EDGE,{"derivedFrom":sQuery(id+"F52.wireOp",EDGE,"E63")}),1.0]])]});
            extrude(context, id + "F53", {"entities" : qUnion([Q0]), "operationType" : NewBodyOperationType.REMOVE, "oppositeDirection" : true, "depth" : 38.1 * mm});
        }
        {
            var Q0;
            Q0=qCreatedBy(makeId("Right.planeOp"),FACE);
            var sketch = newSketch(context, id + "F54", { "sketchPlane" : qUnion([Q0])});
            skLineSegment(sketch, "E64.bottom", {"start": v(45.95, 0) * mm, "end": v(84.05, 0) * mm});
            skLineSegment(sketch, "E64.top", {"start": v(45.95, 184.15) * mm, "end": v(84.05, 184.15) * mm});
            skLineSegment(sketch, "E64.left", {"start": v(45.95, 0) * mm, "end": v(45.95, 184.15) * mm});
            skLineSegment(sketch, "E64.right", {"start": v(84.05, 0) * mm, "end": v(84.05, 184.15) * mm});
            skSolve(sketch);
        }
        {
            var Q0;
            Q0=qSketchRegion(id+"F54",true);
            extrude(context, id + "F55", {"entities" : qUnion([Q0]), "oppositeDirection" : true, "depth" : 2286 * mm});
        }
    });
